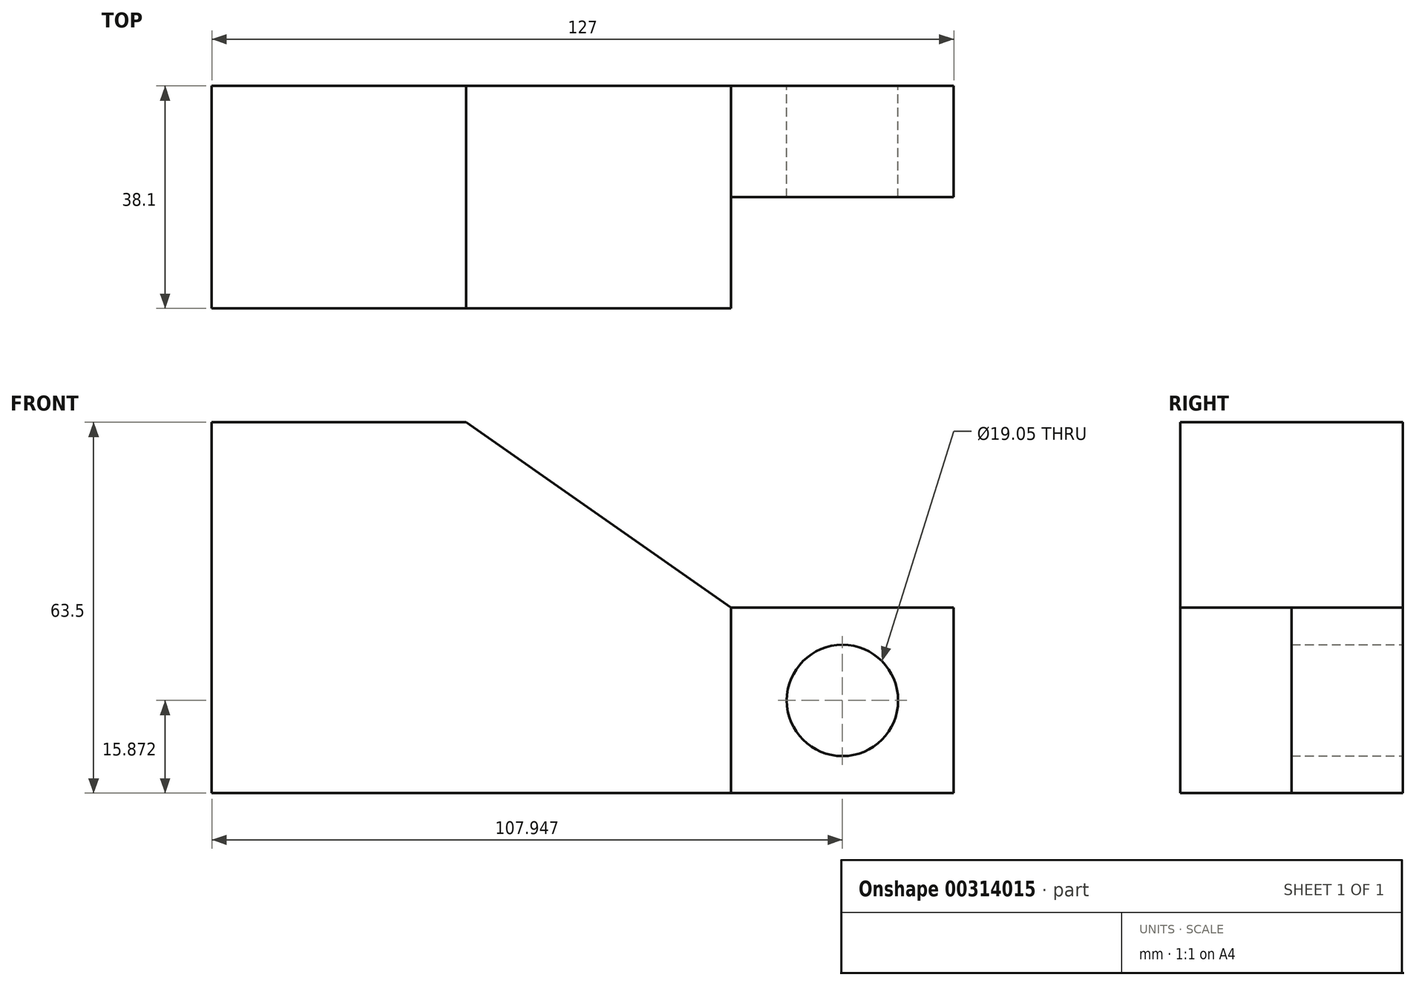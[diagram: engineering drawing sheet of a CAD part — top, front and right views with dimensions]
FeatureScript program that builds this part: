
annotation { "Feature Type Name" : "Feature", "Feature Type Description" : "" }
export const myFeature = defineFeature(function(context is Context, id is Id, definition is map)
    precondition{}
    {
        {
            var Q0;
            Q0=qCreatedBy(makeId("Front.planeOp"),FACE);
            var sketch = newSketch(context, id + "F0", { "sketchPlane" : qUnion([Q0])});
            skLineSegment(sketch, "E0", {"start": v(-57.23, -25.21) * mm, "end": v(69.77, -25.21) * mm});
            skLineSegment(sketch, "E1", {"start": v(-57.23, -25.21) * mm, "end": v(-57.23, 38.29) * mm});
            skLineSegment(sketch, "E2", {"start": v(69.77, -25.21) * mm, "end": v(69.77, 6.54) * mm});
            skLineSegment(sketch, "E3", {"start": v(69.77, 6.54) * mm, "end": v(31.67, 6.54) * mm});
            skLineSegment(sketch, "E4", {"start": v(-57.23, 38.29) * mm, "end": v(-13.7, 38.29) * mm});
            skLineSegment(sketch, "E5", {"start": v(-13.7, 38.29) * mm, "end": v(31.67, 6.54) * mm});
            skLineSegment(sketch, "E6", {"start": v(31.67, 6.54) * mm, "end": v(31.67, -25.21) * mm});
            skPoint(sketch, "E7.centerSnap0", {"position": v(69.77, -9.34) * mm});
            skPoint(sketch, "E7.center.orphan", {"position": v(38.6, -9.34) * mm});
            skCircle(sketch, "E8", {"center": v(50.72, -9.34) * mm, "radius": 9.53 * mm});
            skSolve(sketch);
        }
        {
            var Q0;
            {var subQ0=sQuery(id+"F0.wireOp",EDGE,"E1");Q0=makeQuery(id+"F0.imprint","IMPRINT",FACE,{"disambiguationData":[TD([[makeQuery(id+"F0.imprint","IMPRINT",EDGE,{"derivedFrom":subQ0}),-1.0]])]});}
            extrude(context, id + "F1", {"entities" : qUnion([Q0]), "depth" : 38.1 * mm});
        }
        {
            var Q0;
            {var subQ1=sQuery(id+"F0.wireOp",EDGE,"E2");Q0=makeQuery(id+"F0.imprint","IMPRINT",FACE,{"disambiguationData":[TD([[makeQuery(id+"F0.imprint","IMPRINT",EDGE,{"derivedFrom":subQ1}),1.0]])]});}
            extrude(context, id + "F2", {"entities" : qUnion([Q0]), "operationType" : NewBodyOperationType.ADD, "depth" : 19.05 * mm});
        }
    });
